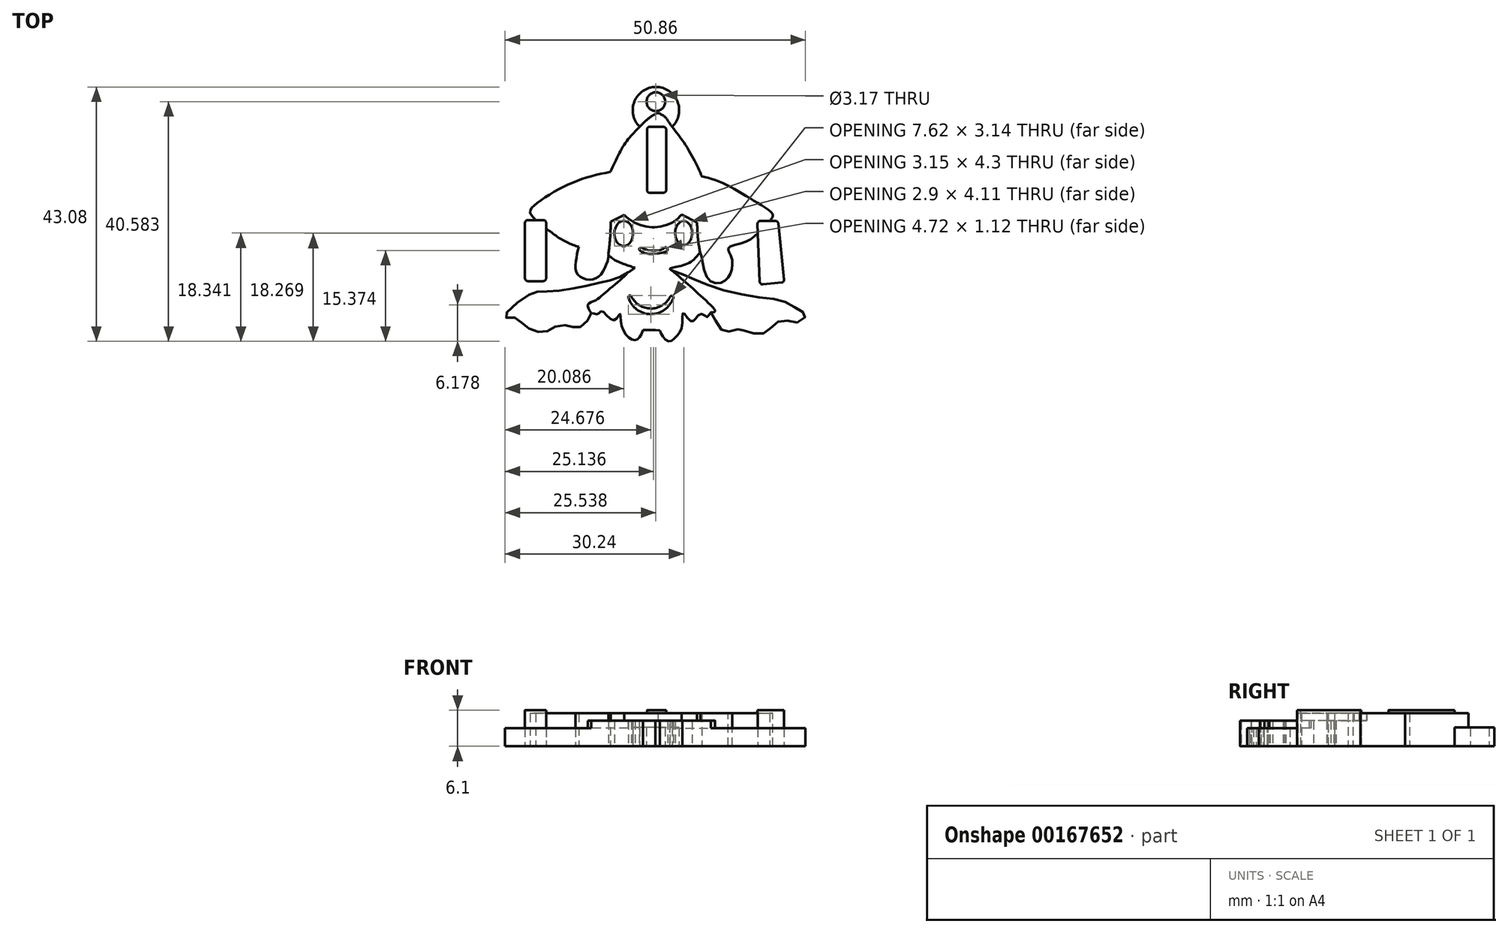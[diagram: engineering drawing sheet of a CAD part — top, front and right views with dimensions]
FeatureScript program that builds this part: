
annotation { "Feature Type Name" : "Feature", "Feature Type Description" : "" }
export const myFeature = defineFeature(function(context is Context, id is Id, definition is map)
    precondition{}
    {
        {
            var Q0;
            Q0=qCreatedBy(makeId("Top.planeOp"),FACE);
            var sketch = newSketch(context, id + "F0", { "sketchPlane" : qUnion([Q0])});
            skFitSpline(sketch, "E0", {"points": [v(-0.45, 12.27) * mm, v(-3.54, 9.93) * mm, v(-6.1, 7) * mm, v(-8.48, 2.31) * mm], "startDerivative": vector(-13, -4.81) * mm, "endDerivative": vector(-5.99, -13.33) * mm});
            skFitSpline(sketch, "E1", {"points": [v(-8.48, 2.31) * mm, v(-12.82, 1.25) * mm, v(-17.12, -0.58) * mm, v(-21.08, -3.14) * mm, v(-22.1, -4.5) * mm, v(-21.12, -5.86) * mm], "startDerivative": vector(-18.77, -3.97) * mm, "endDerivative": vector(10, -9.63) * mm});
            skLineSegment(sketch, "E2", {"start": v(-21.12, -5.86) * mm, "end": v(-19.87, -5.86) * mm});
            skLineSegment(sketch, "E3", {"start": v(-19.38, -6.35) * mm, "end": v(-19.38, -15.72) * mm});
            skLineSegment(sketch, "E4", {"start": v(-19.87, -16.2) * mm, "end": v(-22.47, -16.2) * mm});
            skLineSegment(sketch, "E5", {"start": v(-22.96, -15.72) * mm, "end": v(-22.96, -6.35) * mm});
            skLineSegment(sketch, "E6", {"start": v(-22.47, -5.86) * mm, "end": v(-21.12, -5.86) * mm});
            skPoint(sketch, "E7.visualSharp", {"position": v(-19.38, -5.86) * mm});
            skArc(sketch, "E7.filletArc", {"start": v(-19.38, -6.35) * mm, "mid": v(-19.52, -6) * mm, "end": v(-19.87, -5.86) * mm});
            skPoint(sketch, "E8.visualSharp", {"position": v(-22.96, -5.86) * mm});
            skArc(sketch, "E8.filletArc", {"start": v(-22.47, -5.86) * mm, "mid": v(-22.81, -6) * mm, "end": v(-22.96, -6.35) * mm});
            skPoint(sketch, "E9.visualSharp", {"position": v(-22.96, -16.2) * mm});
            skArc(sketch, "E9.filletArc", {"start": v(-22.96, -15.72) * mm, "mid": v(-22.81, -16.06) * mm, "end": v(-22.47, -16.2) * mm});
            skPoint(sketch, "E10.visualSharp", {"position": v(-19.38, -16.2) * mm});
            skArc(sketch, "E10.filletArc", {"start": v(-19.87, -16.2) * mm, "mid": v(-19.52, -16.06) * mm, "end": v(-19.38, -15.72) * mm});
            skFitSpline(sketch, "E11", {"points": [v(-19.38, -7.27) * mm, v(-16.55, -9.27) * mm, v(-13.87, -10.42) * mm], "startDerivative": vector(5.37, -4.22) * mm, "endDerivative": vector(5.66, -2.05) * mm});
            skFitSpline(sketch, "E12", {"points": [v(-13.87, -10.42) * mm, v(-14.33, -12.75) * mm, v(-14.19, -14.82) * mm, v(-12.72, -15.86) * mm, v(-11, -15.75) * mm, v(-9.6, -14.32) * mm, v(-8.86, -12.28) * mm, v(-8.86, -11.7) * mm], "startDerivative": vector(-3.18, -13.86) * mm, "endDerivative": vector(-0.7, 5.86) * mm});
            skFitSpline(sketch, "E13", {"points": [v(-8.86, -11.7) * mm, v(-8.02, -12.47) * mm, v(-6.35, -13.26) * mm, v(-4.34, -13.95) * mm], "startDerivative": vector(2.7, -2.86) * mm, "endDerivative": vector(5.39, -1.73) * mm});
            skFitSpline(sketch, "E14", {"points": [v(-4.34, -13.95) * mm, v(-5.5, -14.74) * mm, v(-7.6, -15.79) * mm, v(-10.2, -16.47) * mm, v(-14.07, -17.3) * mm, v(-18.49, -17.95) * mm, v(-20.93, -18) * mm, v(-22.96, -18.92) * mm, v(-26.27, -21.87) * mm, v(-26.13, -22.4) * mm, v(-24.53, -22.4) * mm, v(-23.19, -23.62) * mm, v(-21.16, -24.7) * mm, v(-19.19, -24.68) * mm, v(-17.42, -23.79) * mm, v(-15.34, -23.85) * mm, v(-14.3, -24.1) * mm, v(-12.57, -23.26) * mm, v(-11.73, -21.65) * mm, v(-10.65, -21.78) * mm, v(-9.93, -21.32) * mm, v(-7.96, -22.84) * mm, v(-6.88, -21.78) * mm, v(-6.65, -23.56) * mm, v(-5.15, -25.91) * mm, v(-3.94, -26.1) * mm, v(-2.97, -24.51) * mm], "startDerivative": vector(-32.77, -24.05) * mm, "endDerivative": vector(22.07, 54.76) * mm});
            skLineSegment(sketch, "E15", {"start": v(-2.97, -24.51) * mm, "end": v(-0.87, -24.51) * mm});
            skFitSpline(sketch, "E16", {"points": [v(-0.45, 12.27) * mm, v(1.52, 10.55) * mm, v(4.05, 7.09) * mm, v(6.42, 2.83) * mm, v(6.96, 1.55) * mm], "startDerivative": vector(15.94, -5.31) * mm, "endDerivative": vector(2.4, -6.69) * mm});
            skFitSpline(sketch, "E17", {"points": [v(6.96, 1.55) * mm, v(9.01, 1) * mm, v(11.77, -0.22) * mm, v(14.74, -1.94) * mm, v(17.75, -3.8) * mm, v(19, -4.98) * mm, v(18.5, -6.02) * mm], "startDerivative": vector(12.7, -2.86) * mm, "endDerivative": vector(-7.2, -9.2) * mm});
            skLineSegment(sketch, "E18", {"start": v(18.5, -6.02) * mm, "end": v(19.45, -6.02) * mm});
            skLineSegment(sketch, "E19", {"start": v(19.94, -6.46) * mm, "end": v(20.92, -15.91) * mm});
            skLineSegment(sketch, "E20", {"start": v(20.48, -16.45) * mm, "end": v(17.33, -16.77) * mm});
            skLineSegment(sketch, "E21", {"start": v(16.4, -6.53) * mm, "end": v(16.8, -16.3) * mm});
            skLineSegment(sketch, "E22", {"start": v(16.9, -6.02) * mm, "end": v(18.5, -6.02) * mm});
            skPoint(sketch, "E23.visualSharp", {"position": v(16.39, -6.02) * mm});
            skArc(sketch, "E23.filletArc", {"start": v(16.9, -6.02) * mm, "mid": v(16.54, -6.17) * mm, "end": v(16.4, -6.53) * mm});
            skPoint(sketch, "E24.visualSharp", {"position": v(16.81, -16.83) * mm});
            skArc(sketch, "E24.filletArc", {"start": v(16.8, -16.3) * mm, "mid": v(16.96, -16.66) * mm, "end": v(17.33, -16.77) * mm});
            skPoint(sketch, "E25.visualSharp", {"position": v(20.97, -16.4) * mm});
            skArc(sketch, "E25.filletArc", {"start": v(20.48, -16.45) * mm, "mid": v(20.81, -16.27) * mm, "end": v(20.92, -15.91) * mm});
            skPoint(sketch, "E26.visualSharp", {"position": v(19.9, -6.02) * mm});
            skArc(sketch, "E26.filletArc", {"start": v(19.94, -6.46) * mm, "mid": v(19.78, -6.14) * mm, "end": v(19.45, -6.02) * mm});
            skFitSpline(sketch, "E27", {"points": [v(16.47, -8.12) * mm, v(14.22, -9.63) * mm, v(11.48, -10.6) * mm, v(11.97, -12.04) * mm, v(11.97, -14.5) * mm, v(10.68, -16.28) * mm, v(7.94, -15.74) * mm, v(6.71, -11.45) * mm, v(5.2, -12.9) * mm, v(1.61, -14.13) * mm, v(3.55, -15) * mm, v(7.68, -16.76) * mm, v(15.88, -18.85) * mm, v(20.82, -19.6) * mm, v(23.44, -21.1) * mm, v(24.53, -21.96) * mm, v(23.23, -23.2) * mm, v(20.66, -22.82) * mm, v(18.46, -24.27) * mm, v(16.95, -25.18) * mm, v(14.11, -24.6) * mm, v(13.2, -24.38) * mm, v(11.16, -24.75) * mm, v(9.71, -23.68) * mm, v(8.48, -21.54) * mm, v(7.96, -22.27) * mm, v(6.94, -21.79) * mm, v(5.8, -22.7) * mm, v(5.07, -22.96) * mm, v(3.84, -21.6) * mm, v(3.66, -23.72) * mm, v(2.66, -25.55) * mm, v(1.55, -26.4) * mm, v(0.44, -25.7) * mm, v(-0.1, -24.53) * mm], "startDerivative": vector(-58.23, -53.74) * mm, "endDerivative": vector(-17.55, 54.23) * mm});
            skLineSegment(sketch, "E28", {"start": v(-0.87, -24.51) * mm, "end": v(-0.1, -24.53) * mm});
            skFitSpline(sketch, "E29", {"points": [v(-8.86, -11.7) * mm, v(-8.6, -9.66) * mm, v(-8.42, -6.15) * mm], "startDerivative": vector(0.62, 4.4) * mm, "endDerivative": vector(0.27, 6.62) * mm});
            skFitSpline(sketch, "E30", {"points": [v(6.71, -11.45) * mm, v(6.32, -9) * mm, v(6.18, -6.27) * mm], "startDerivative": vector(-0.92, 4.96) * mm, "endDerivative": vector(-0.15, 5.4) * mm});
            skLineSegment(sketch, "E31", {"start": v(-8.42, -6.15) * mm, "end": v(-6.15, -5) * mm});
            skLineSegment(sketch, "E32", {"start": v(6.18, -6.27) * mm, "end": v(3.53, -4.95) * mm});
            skFitSpline(sketch, "E33", {"points": [v(-6.15, -5) * mm, v(-4.64, -6.17) * mm, v(-2.28, -7) * mm, v(-0.03, -6.98) * mm, v(2.3, -6.1) * mm, v(3.53, -4.95) * mm], "startDerivative": vector(7.24, -6.6) * mm, "endDerivative": vector(5.95, 6.88) * mm});
            skEllipse(sketch, "E34", {"center": v(-6.24, -8.13) * mm, "majorRadius": 2.15 * mm, "minorRadius": 1.58 * mm, "majorAxis": v(0, 1)});
            skEllipse(sketch, "E35", {"center": v(3.91, -8.06) * mm, "majorRadius": 2.05 * mm, "minorRadius": 1.45 * mm, "majorAxis": v(0, 1)});
            skFitSpline(sketch, "E36", {"points": [v(-3.19, -10.54) * mm, v(-2.61, -10.83) * mm, v(0.25, -10.85) * mm, v(0.83, -10.45) * mm, v(1.19, -10.83) * mm, v(0.5, -11.36) * mm, v(-2.92, -11.4) * mm, v(-3.62, -10.69) * mm, v(-3.19, -10.54) * mm]});
            skFitSpline(sketch, "E37", {"points": [v(-5.5, -14.74) * mm, v(-7.32, -16.45) * mm, v(-9.6, -18.36) * mm, v(-11, -19.46) * mm, v(-12.29, -20.17) * mm, v(-11.73, -21.65) * mm], "startDerivative": vector(-7.68, -7.5) * mm, "endDerivative": vector(6.08, -9.56) * mm});
            skFitSpline(sketch, "E38", {"points": [v(1.61, -14.13) * mm, v(4.34, -16.5) * mm, v(7.83, -19.65) * mm, v(9.21, -21.32) * mm, v(8.48, -21.54) * mm], "startDerivative": vector(8.87, -7.6) * mm, "endDerivative": vector(-7.47, -0.5) * mm});
            skLineSegment(sketch, "E39.bottom", {"start": v(-1.82, 9.93) * mm, "end": v(0.46, 9.93) * mm});
            skLineSegment(sketch, "E39.top", {"start": v(-1.82, -1.26) * mm, "end": v(0.46, -1.26) * mm});
            skLineSegment(sketch, "E39.left", {"start": v(-2.3, 9.44) * mm, "end": v(-2.3, -0.77) * mm});
            skLineSegment(sketch, "E39.right", {"start": v(0.95, 9.44) * mm, "end": v(0.95, -0.77) * mm});
            skPoint(sketch, "E40.visualSharp", {"position": v(-2.3, 9.93) * mm});
            skArc(sketch, "E40.filletArc", {"start": v(-1.82, 9.93) * mm, "mid": v(-2.16, 9.79) * mm, "end": v(-2.3, 9.44) * mm});
            skPoint(sketch, "E41.visualSharp", {"position": v(0.95, 9.93) * mm});
            skArc(sketch, "E41.filletArc", {"start": v(0.95, 9.44) * mm, "mid": v(0.8, 9.79) * mm, "end": v(0.46, 9.93) * mm});
            skPoint(sketch, "E42.visualSharp", {"position": v(-2.3, -1.26) * mm});
            skArc(sketch, "E42.filletArc", {"start": v(-2.3, -0.77) * mm, "mid": v(-2.16, -1.11) * mm, "end": v(-1.82, -1.26) * mm});
            skPoint(sketch, "E43.visualSharp", {"position": v(0.95, -1.26) * mm});
            skArc(sketch, "E43.filletArc", {"start": v(0.46, -1.26) * mm, "mid": v(0.8, -1.11) * mm, "end": v(0.95, -0.77) * mm});
            skArc(sketch, "E44", {"start": v(1.96, 9.93) * mm, "mid": v(-0.8, 16.68) * mm, "end": v(-3.54, 9.93) * mm});
            skCircle(sketch, "E45", {"center": v(-0.8, 14.18) * mm, "radius": 1.59 * mm});
            skArc(sketch, "E46", {"start": v(-4.92, -18.85) * mm, "mid": v(-1.68, -20.85) * mm, "end": v(1.6, -18.9) * mm});
            skArc(sketch, "E47", {"start": v(-5.46, -18.99) * mm, "mid": v(-1.7, -21.8) * mm, "end": v(2.14, -19.08) * mm});
            skArc(sketch, "E48", {"start": v(2.14, -19.08) * mm, "mid": v(1.96, -18.7) * mm, "end": v(1.6, -18.9) * mm});
            skArc(sketch, "E49", {"start": v(-4.92, -18.85) * mm, "mid": v(-5.26, -18.66) * mm, "end": v(-5.46, -18.99) * mm});
            skSolve(sketch);
        }
        {
            var Q0;
            {var subQ11=sQuery(id+"F0.wireOp",EDGE,"E1");Q0=makeQuery(id+"F0.imprint","IMPRINT",FACE,{"disambiguationData":[TD([[makeQuery(id+"F0.imprint","IMPRINT",EDGE,{"derivedFrom":subQ11}),1.0]])]});}
            extrude(context, id + "F1", {"entities" : qUnion([Q0]), "depth" : 5.6 * mm});
        }
        {
            var Q0;
            {var subQ11=sQuery(id+"F0.wireOp",EDGE,"E13");Q0=makeQuery(id+"F0.imprint","IMPRINT",FACE,{"disambiguationData":[TD([[makeQuery(id+"F0.imprint","IMPRINT",EDGE,{"derivedFrom":subQ11}),1.0]])]});}
            extrude(context, id + "F2", {"entities" : qUnion([Q0]), "operationType" : NewBodyOperationType.ADD, "depth" : 4.32 * mm});
        }
        {
            var Q0;
            {var subQ0=sQuery(id+"F0.wireOp",EDGE,"E37");Q0=makeQuery(id+"F0.imprint","IMPRINT",FACE,{"disambiguationData":[TD([[makeQuery(id+"F0.imprint","IMPRINT",EDGE,{"derivedFrom":subQ0}),-1.0]])]});}
            var Q1;
            {var subQ0=sQuery(id+"F0.wireOp",EDGE,"E38");var subQ1=sQuery(id+"F0.wireOp",EDGE,"E27");var subQ2=makeQuery(id+"F0.imprint","INTERSECT",VERTEX,{"disambiguationData":[OD(2.0)],"derivedFrom":[subQ1,subQ0]});Q1=makeQuery(id+"F0.imprint","IMPRINT",FACE,{"disambiguationData":[TD([[makeQuery(id+"F0.imprint","IMPRINT",EDGE,{"disambiguationData":[TD([[subQ2,-1.0]])],"derivedFrom":subQ1}),-1.0]])]});}
            extrude(context, id + "F3", {"entities" : qUnion([Q0, Q1]), "operationType" : NewBodyOperationType.ADD, "depth" : 3.05 * mm});
        }
        {
            var Q0;
            Q0=makeQuery(id+"F0.imprint","IMPRINT",FACE,{"disambiguationData":[TD([[makeQuery(id+"F0.imprint","IMPRINT",EDGE,{"derivedFrom":sQuery(id+"F0.wireOp",EDGE,"E2")}),-1.0]])]});
            var Q1;
            Q1=makeQuery(id+"F0.imprint","IMPRINT",FACE,{"disambiguationData":[TD([[makeQuery(id+"F0.imprint","IMPRINT",EDGE,{"derivedFrom":sQuery(id+"F0.wireOp",EDGE,"E18")}),-1.0]])]});
            var Q2;
            Q2=makeQuery(id+"F0.imprint","IMPRINT",FACE,{"disambiguationData":[TD([[makeQuery(id+"F0.imprint","IMPRINT",EDGE,{"derivedFrom":sQuery(id+"F0.wireOp",EDGE,"E39.bottom")}),-1.0]])]});
            extrude(context, id + "F4", {"entities" : qUnion([Q0, Q1, Q2]), "operationType" : NewBodyOperationType.ADD, "depth" : 6.1 * mm});
        }
        {
            var Q0;
            {var subQ3=sQuery(id+"F0.wireOp",EDGE,"E44");Q0=makeQuery(id+"F0.imprint","IMPRINT",FACE,{"disambiguationData":[TD([[makeQuery(id+"F0.imprint","IMPRINT",EDGE,{"derivedFrom":subQ3}),1.0]])]});}
            extrude(context, id + "F5", {"entities" : qUnion([Q0]), "operationType" : NewBodyOperationType.ADD, "depth" : 3.17 * mm});
        }
    });
